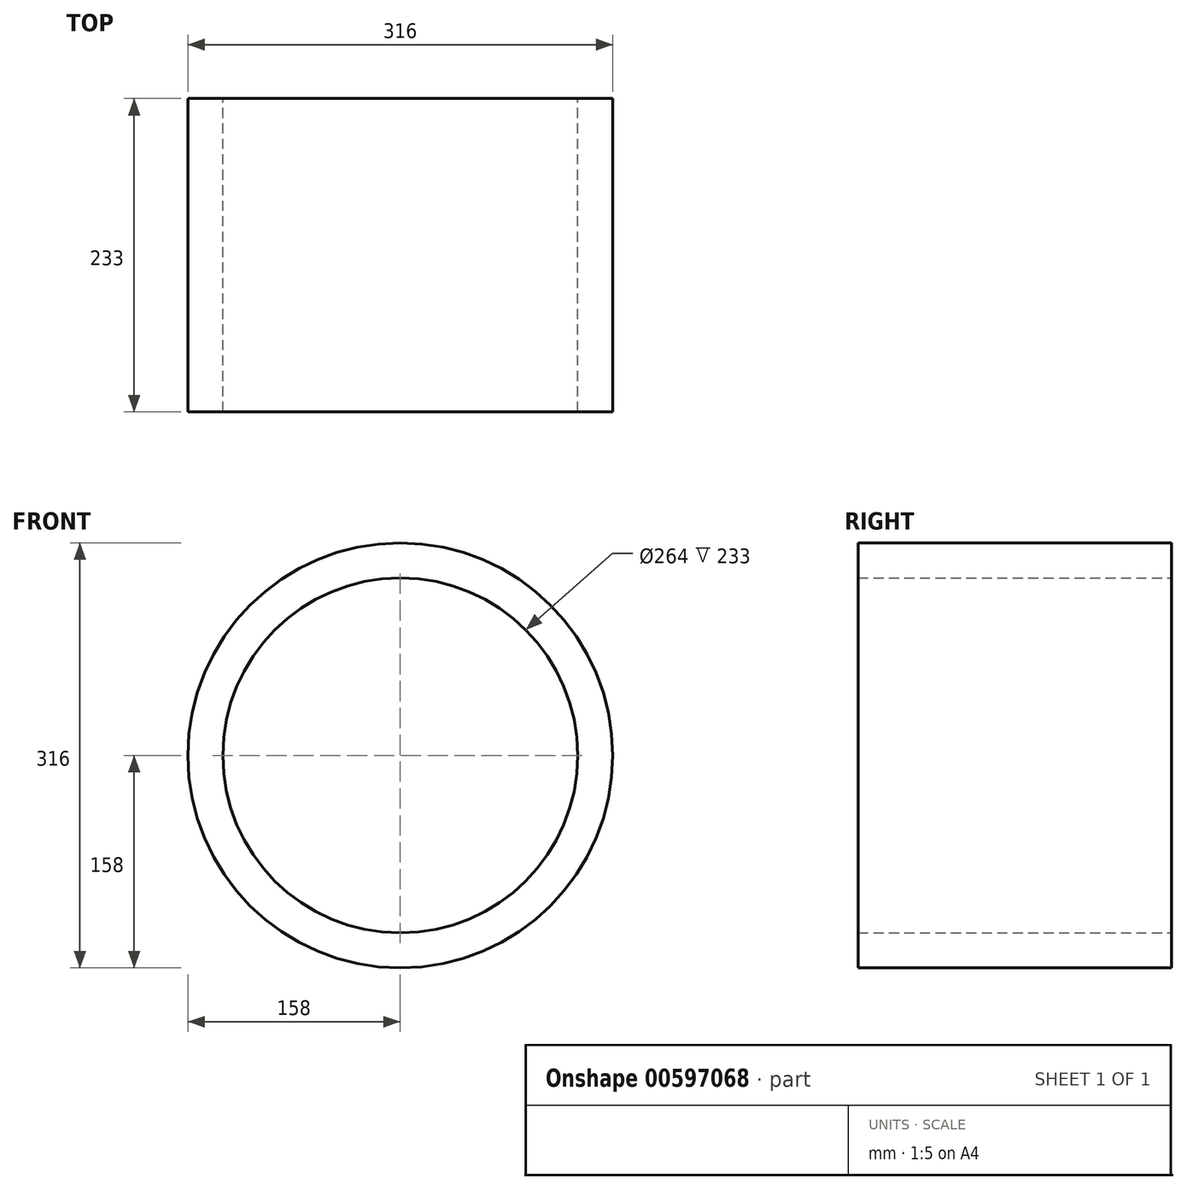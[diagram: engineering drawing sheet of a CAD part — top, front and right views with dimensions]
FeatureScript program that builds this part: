
annotation { "Feature Type Name" : "Feature", "Feature Type Description" : "" }
export const myFeature = defineFeature(function(context is Context, id is Id, definition is map)
    precondition{}
    {
        {
            var Q0;
            Q0=qCreatedBy(makeId("Front.planeOp"),FACE);
            var sketch = newSketch(context, id + "F0", { "sketchPlane" : qUnion([Q0])});
            skCircle(sketch, "E0", {"center": v(0, 0) * mm, "radius": 132 * mm});
            skSolve(sketch);
        }
        {
            var Q0;
            Q0=makeQuery(id+"F0.imprint","IMPRINT",FACE,{"disambiguationData":[TD([[makeQuery(id+"F0.imprint","IMPRINT",EDGE,{"derivedFrom":sQuery(id+"F0.wireOp",EDGE,"E0")}),1.0]])]});
            var sketch = newSketch(context, id + "F1", { "sketchPlane" : qUnion([Q0])});
            skCircle(sketch, "E1", {"center": v(0, 0) * mm, "radius": 158 * mm});
            skSolve(sketch);
        }
        {
            var Q0;
            Q0 = qSketchRegion(id + "F1", true);
            extrude(context, id + "F2", {"entities" : qUnion([Q0]), "depth" : 233 * mm, "offsetDistance" : 25 * mm});
        }
        {
            var Q0;
            Q0=makeQuery(id+"F0.imprint","IMPRINT",FACE,{"disambiguationData":[TD([[makeQuery(id+"F0.imprint","IMPRINT",EDGE,{"derivedFrom":sQuery(id+"F0.wireOp",EDGE,"E0")}),1.0]])]});
            var Q1;
            Q1=sQuery(id+"F0.wireOp",EDGE,"E0");
            extrude(context, id + "F3", {"entities" : qUnion([Q0]), "operationType" : NewBodyOperationType.REMOVE, "surfaceEntities" : qUnion([Q1]), "depth" : 233 * mm, "offsetDistance" : 25 * mm});
        }
    });
